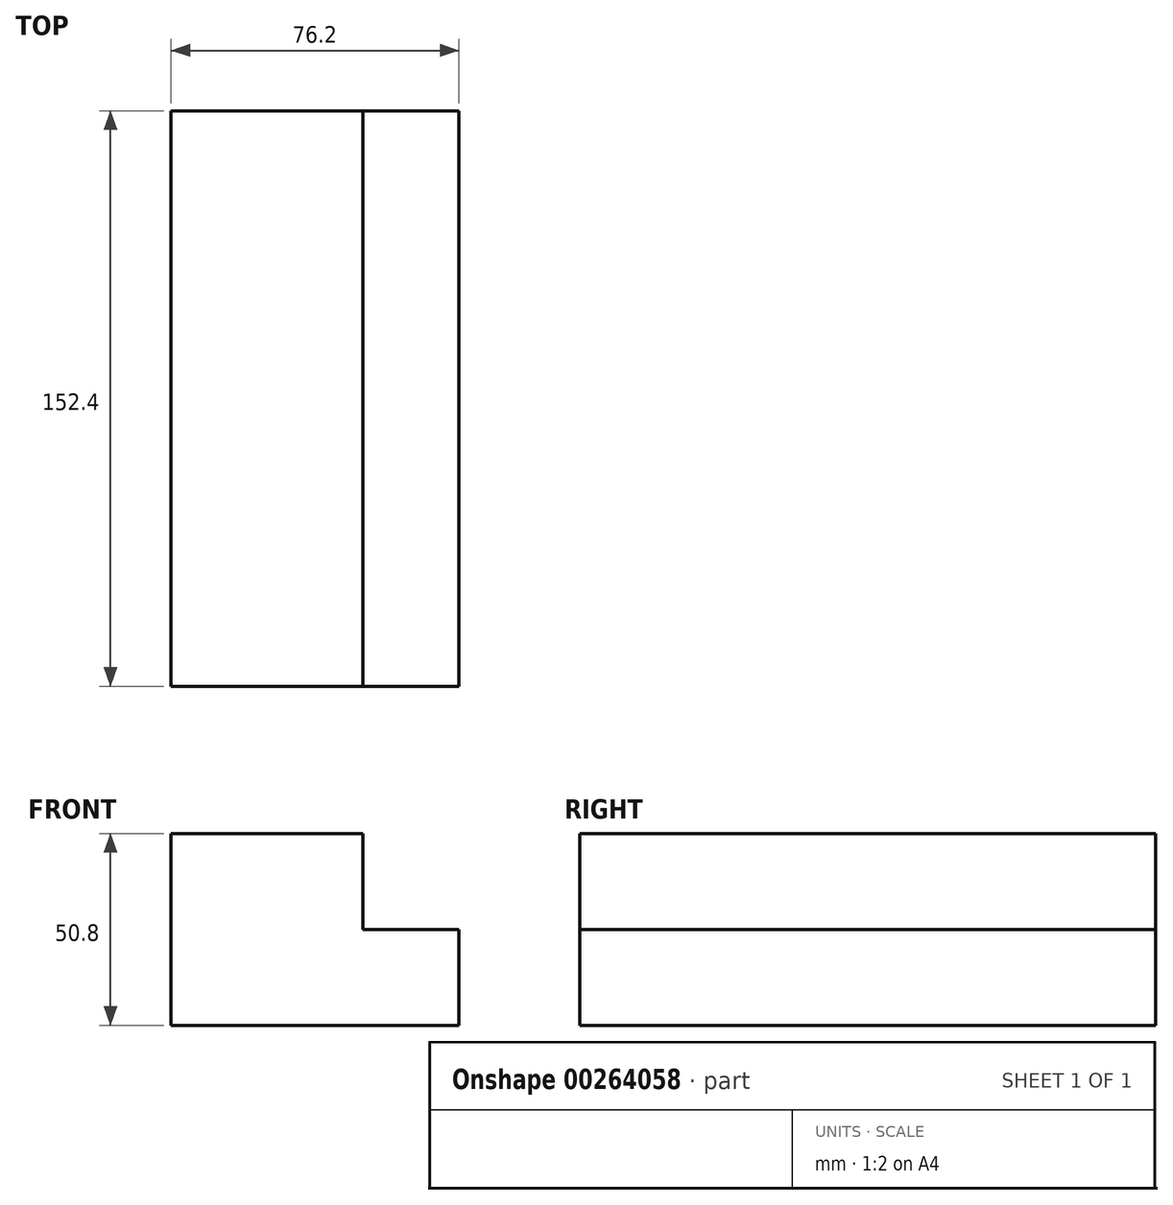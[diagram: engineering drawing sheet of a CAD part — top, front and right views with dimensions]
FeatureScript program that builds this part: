
annotation { "Feature Type Name" : "Feature", "Feature Type Description" : "" }
export const myFeature = defineFeature(function(context is Context, id is Id, definition is map)
    precondition{}
    {
        {
            var Q0;
            Q0=qCreatedBy(makeId("Front.planeOp"),FACE);
            var sketch = newSketch(context, id + "F0", { "sketchPlane" : qUnion([Q0])});
            skLineSegment(sketch, "E0", {"start": v(-40.57, -26.75) * mm, "end": v(35.63, -26.75) * mm});
            skLineSegment(sketch, "E1", {"start": v(-40.57, -26.75) * mm, "end": v(-40.57, 24.05) * mm});
            skLineSegment(sketch, "E2", {"start": v(-40.57, 24.05) * mm, "end": v(10.23, 24.05) * mm});
            skLineSegment(sketch, "E3", {"start": v(10.23, 24.05) * mm, "end": v(10.23, -1.35) * mm});
            skLineSegment(sketch, "E4", {"start": v(10.23, -1.35) * mm, "end": v(35.63, -1.35) * mm});
            skLineSegment(sketch, "E5", {"start": v(35.63, -1.35) * mm, "end": v(35.63, -26.75) * mm});
            skSolve(sketch);
        }
        {
            var Q0;
            Q0 = qSketchRegion(id + "F0", true);
            extrude(context, id + "F1", {"entities" : qUnion([Q0]), "depth" : 152.4 * mm});
        }
    });
